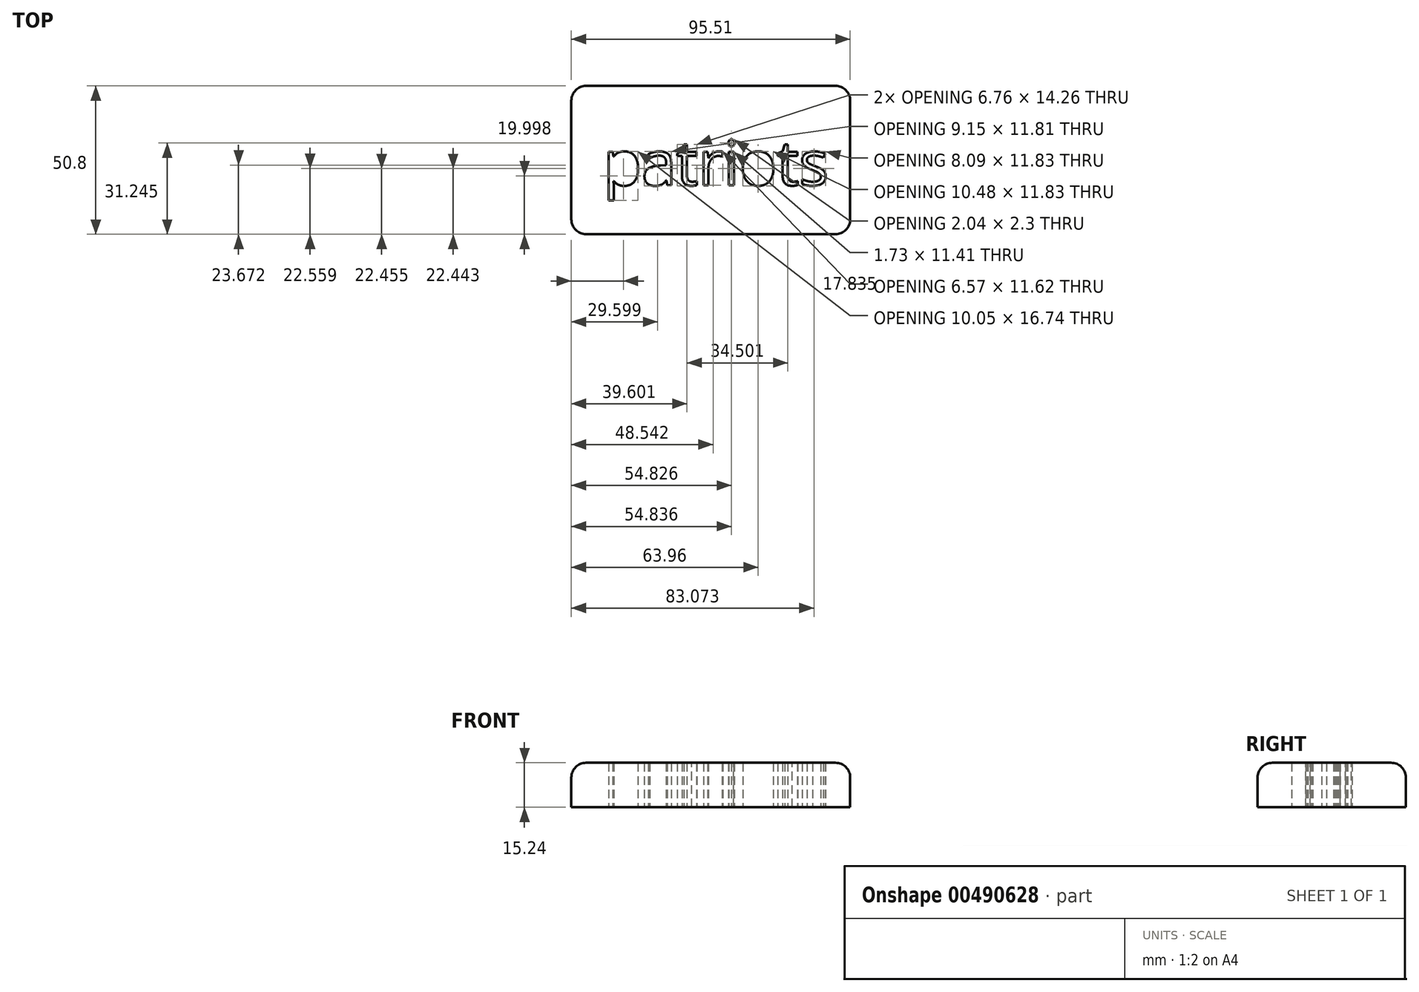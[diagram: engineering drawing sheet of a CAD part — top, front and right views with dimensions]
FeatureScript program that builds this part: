
annotation { "Feature Type Name" : "Feature", "Feature Type Description" : "" }
export const myFeature = defineFeature(function(context is Context, id is Id, definition is map)
    precondition{}
    {
        {
            var Q0;
            Q0=qCreatedBy(makeId("Top.planeOp"),FACE);
            var sketch = newSketch(context, id + "F0", { "sketchPlane" : qUnion([Q0])});
            skText(sketch, "E0", { "text": "patriots", "fontName": "OpenSans-Regular.ttf"});
            skLineSegment(sketch, "E1.bottom", {"start": v(-88.52, 56.97) * mm, "end": v(6.99, 56.97) * mm});
            skLineSegment(sketch, "E1.top", {"start": v(-88.52, 6.17) * mm, "end": v(6.99, 6.17) * mm});
            skLineSegment(sketch, "E1.left", {"start": v(-88.52, 56.97) * mm, "end": v(-88.52, 6.17) * mm});
            skLineSegment(sketch, "E1.right", {"start": v(6.99, 56.97) * mm, "end": v(6.99, 6.17) * mm});
            const initialGuessF0  = {"E0": [-0.07754, 0.02292, 1, 0, 0.01535]};
            skSetInitialGuess(sketch, initialGuessF0);
            skSolve(sketch);
        }
        {
            var Q0;
            Q0=makeQuery(id+"F0.imprint","IMPRINT",FACE,{"disambiguationData":[TD([[makeQuery(id+"F0.imprint","IMPRINT",EDGE,{"derivedFrom":sQuery(id+"F0.wireOp",EDGE,"E0.sketch_text.stroke-0")}),1.0]])]});
            extrude(context, id + "F1", {"entities" : qUnion([Q0]), "depth" : 15.24 * mm});
        }
        {
            var Q0;
            Q0=makeQuery(id+"F1.opExtrude","SWEPT_EDGE",EDGE,{"disambiguationData":[OSD([sQuery(id+"F0.wireOp",EDGE,"E1.bottom"),sQuery(id+"F0.wireOp",EDGE,"E1.right")])]});
            var Q1;
            Q1=makeQuery(id+"F1.opExtrude","CAP_EDGE",EDGE,{"disambiguationData":[OSD([sQuery(id+"F0.wireOp",EDGE,"E1.bottom")])],"isStart":false});
            var Q2;
            Q2=makeQuery(id+"F1.opExtrude","CAP_EDGE",EDGE,{"disambiguationData":[OSD([sQuery(id+"F0.wireOp",EDGE,"E1.right")])],"isStart":false});
            var Q3;
            Q3=makeQuery(id+"F1.opExtrude","SWEPT_EDGE",EDGE,{"disambiguationData":[OSD([sQuery(id+"F0.wireOp",EDGE,"E1.top"),sQuery(id+"F0.wireOp",EDGE,"E1.right")])]});
            var Q4;
            Q4=makeQuery(id+"F1.opExtrude","CAP_EDGE",EDGE,{"disambiguationData":[OSD([sQuery(id+"F0.wireOp",EDGE,"E1.top")])],"isStart":false});
            var Q5;
            Q5=makeQuery(id+"F1.opExtrude","SWEPT_EDGE",EDGE,{"disambiguationData":[OSD([sQuery(id+"F0.wireOp",EDGE,"E1.top"),sQuery(id+"F0.wireOp",EDGE,"E1.left")])]});
            var Q6;
            Q6=makeQuery(id+"F1.opExtrude","SWEPT_EDGE",EDGE,{"disambiguationData":[OSD([sQuery(id+"F0.wireOp",EDGE,"E1.bottom"),sQuery(id+"F0.wireOp",EDGE,"E1.left")])]});
            var Q7;
            Q7=makeQuery(id+"F1.opExtrude","CAP_EDGE",EDGE,{"disambiguationData":[OSD([sQuery(id+"F0.wireOp",EDGE,"E1.left")])],"isStart":false});
            fillet(context, id + "F2", {"entities" : qUnion([Q0, Q1, Q2, Q3, Q4, Q5, Q6, Q7]), "radius" : 5.08 * mm, "tangentPropagation" : true, "allowEdgeOverflow" : false});
        }
    });
